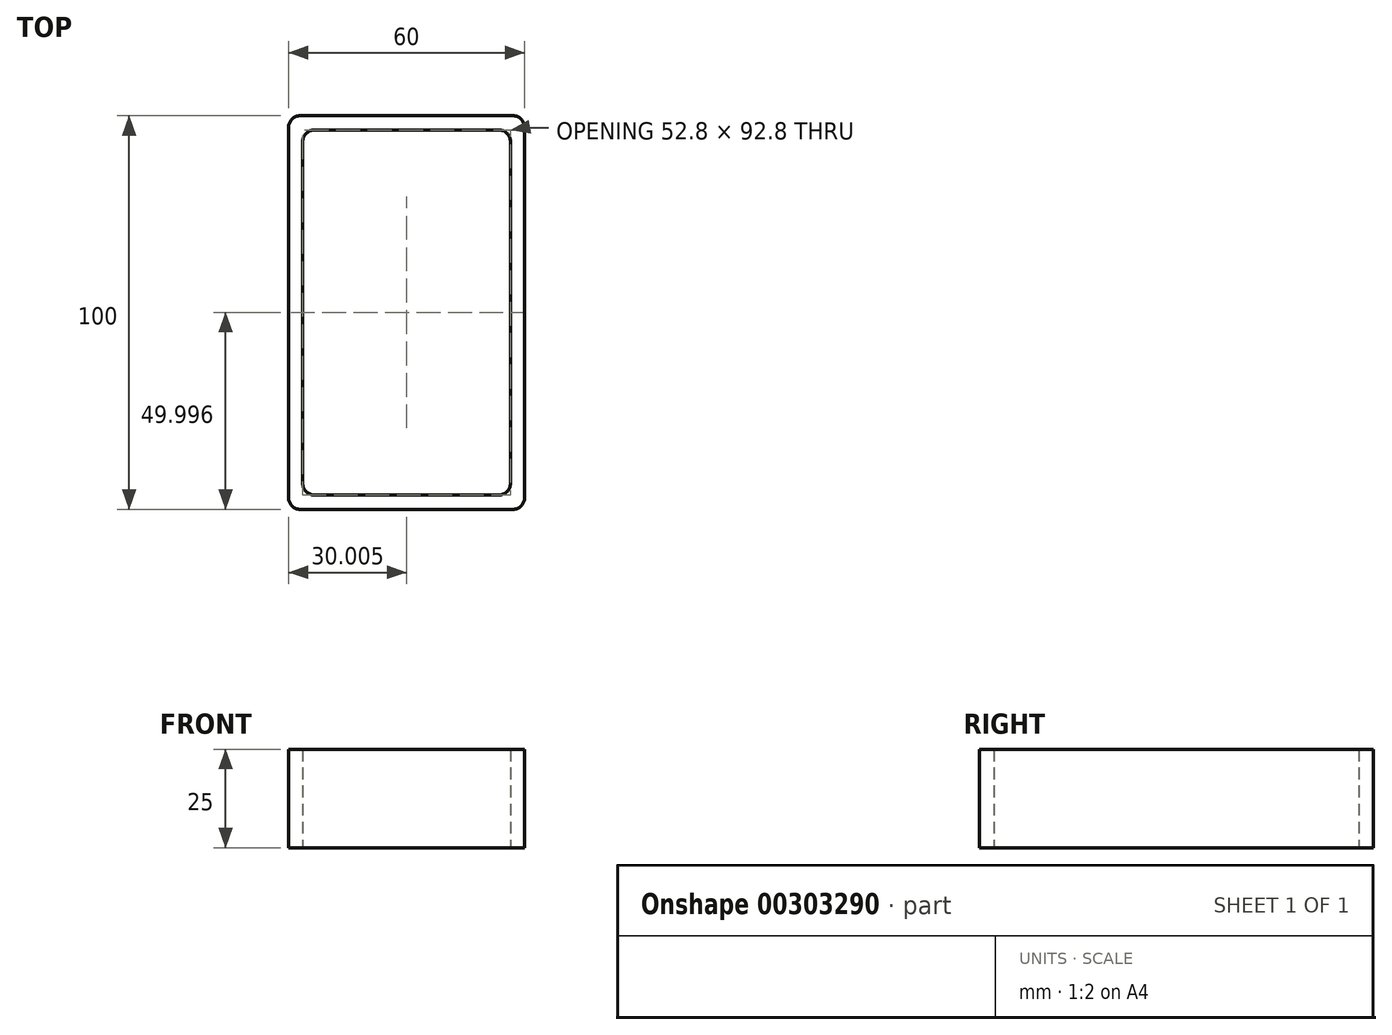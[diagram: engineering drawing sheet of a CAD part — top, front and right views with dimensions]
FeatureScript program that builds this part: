
annotation { "Feature Type Name" : "Feature", "Feature Type Description" : "" }
export const myFeature = defineFeature(function(context is Context, id is Id, definition is map)
    precondition{}
    {
        {
            var Q0;
            Q0=qCreatedBy(makeId("Top.planeOp"),FACE);
            var sketch = newSketch(context, id + "F0", { "sketchPlane" : qUnion([Q0])});
            skLineSegment(sketch, "E0.bottom", {"start": v(-41.94, 64.8) * mm, "end": v(12.06, 64.8) * mm});
            skLineSegment(sketch, "E0.top", {"start": v(-41.94, -35.2) * mm, "end": v(12.06, -35.2) * mm});
            skLineSegment(sketch, "E0.left", {"start": v(-44.94, 61.8) * mm, "end": v(-44.94, -32.2) * mm});
            skLineSegment(sketch, "E0.right", {"start": v(15.06, 61.8) * mm, "end": v(15.06, -32.2) * mm});
            skLineSegment(sketch, "E1.bottom", {"start": v(-38.34, 61.2) * mm, "end": v(8.46, 61.2) * mm});
            skLineSegment(sketch, "E1.top", {"start": v(-38.34, -31.6) * mm, "end": v(8.46, -31.6) * mm});
            skLineSegment(sketch, "E1.left", {"start": v(-41.34, 58.2) * mm, "end": v(-41.34, -28.6) * mm});
            skLineSegment(sketch, "E1.right", {"start": v(11.46, 58.2) * mm, "end": v(11.46, -28.6) * mm});
            skPoint(sketch, "E2.visualSharp", {"position": v(-41.34, 61.2) * mm});
            skArc(sketch, "E2.filletArc", {"start": v(-38.34, 61.2) * mm, "mid": v(-40.46, 60.33) * mm, "end": v(-41.34, 58.2) * mm});
            skPoint(sketch, "E3.visualSharp", {"position": v(-44.94, 64.8) * mm});
            skArc(sketch, "E3.filletArc", {"start": v(-41.94, 64.8) * mm, "mid": v(-44.06, 63.93) * mm, "end": v(-44.94, 61.8) * mm});
            skPoint(sketch, "E4.visualSharp", {"position": v(11.46, 61.2) * mm});
            skArc(sketch, "E4.filletArc", {"start": v(11.46, 58.2) * mm, "mid": v(10.59, 60.33) * mm, "end": v(8.46, 61.2) * mm});
            skPoint(sketch, "E5.visualSharp", {"position": v(15.06, 64.8) * mm});
            skArc(sketch, "E5.filletArc", {"start": v(15.06, 61.8) * mm, "mid": v(14.19, 63.93) * mm, "end": v(12.06, 64.8) * mm});
            skPoint(sketch, "E6.visualSharp", {"position": v(11.46, -31.6) * mm});
            skArc(sketch, "E6.filletArc", {"start": v(8.46, -31.6) * mm, "mid": v(10.59, -30.72) * mm, "end": v(11.46, -28.6) * mm});
            skPoint(sketch, "E7.visualSharp", {"position": v(15.06, -35.2) * mm});
            skArc(sketch, "E7.filletArc", {"start": v(12.06, -35.2) * mm, "mid": v(14.19, -34.32) * mm, "end": v(15.06, -32.2) * mm});
            skPoint(sketch, "E8.visualSharp", {"position": v(-41.34, -31.6) * mm});
            skArc(sketch, "E8.filletArc", {"start": v(-41.34, -28.6) * mm, "mid": v(-40.46, -30.72) * mm, "end": v(-38.34, -31.6) * mm});
            skPoint(sketch, "E9.visualSharp", {"position": v(-44.94, -35.2) * mm});
            skArc(sketch, "E9.filletArc", {"start": v(-44.94, -32.2) * mm, "mid": v(-44.06, -34.32) * mm, "end": v(-41.94, -35.2) * mm});
            skSolve(sketch);
        }
        {
            var Q0;
            Q0 = qSketchRegion(id + "F0", true);
            extrude(context, id + "F1", {"entities" : qUnion([Q0]), "depth" : 25 * mm});
        }
    });
